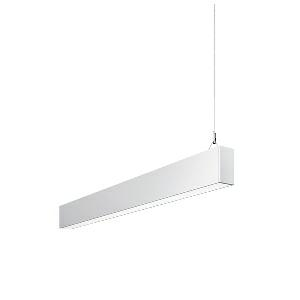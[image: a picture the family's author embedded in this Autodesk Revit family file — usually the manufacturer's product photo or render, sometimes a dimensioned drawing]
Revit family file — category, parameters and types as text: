
# Revit family: idoo_line_-_ilp_3000_840_d_end_00805690_544f
name_source: partatom
category: Lighting Fixtures
units: mm (PartAtom-declared; Revit-internal decimal feet)

## family parameters
Cut with Voids When Loaded = No
Host = Face
Light Source = No
Part Type = Normal
Room Calculation Point = No
Round Connector Dimension = Use Diameter
Shared = No

## types (1)
- IDOO.line - ILP 3000/840/D END (1 x LED, 3150 lm, 4000K)
    Apparent Load = 23 VA
    Approval mark = CE
    CIE Flux Codes = 66 91 98 40 100
    Color Rendering = 80-89
    Color Temperature = 4000K
    Control Gear = Electronic ballast
    Default Elevation = 1800 mm
    Description = ILP 3000/840/D|Suspended luminaire|light source: LED|connected load: 220-240 V, 50/60 Hz|Power consumption: approx. 23 W|standby: approx. 0,20|luminous flux: 3150 lm|luminous efficacy: 136 lm/W|light distribution: Direct/indirect|direct ratio: approx. 40 %|colour temperature: Cold white, ca. 4000 K|color rendering index (CRI): >= 80|chromaticity tolerance:  3 SDCM|System of protection: IP 40|technology: Continuously dimmable|luminaire body|material: Sectional aluminium|colour: White|lamp cover: Acrylic (PMMA), Clear|mains lead: 1,0 m With free stranded wires|Fastening: Steel cable 0.3 - 0.7 m|glare control: Prism aperture|luminance(L65): <= 2700 cd/m|unified glare rating(4H 8H): <=  16|special features: DALI Load 1x, TouchDIM - dimming via standard switch, Through-wired, up to 18 m on one mains connection, Flicker-free, Suitable as emergency lighting, Mechanical and electrical connection of the individual modules without tools|
    Frequency = 50 Hz
    Height = 110 mm
    Lamp = 1 x LED
    Lamp Light Flux = 3150 lm
    Lamp count = 1
    Length = 1128 mm
    Luminous efficacy = 137 lm/W
    Manufacturer = Waldmann
    ModVariant = No
    Model = 00805690
    Mounting Place = Ceiling
    Mounting Type = Pendant
    Number of Poles = 1
    OnlyDefault = Yes
    Power Factor = 1
    Product Name = IDOO.line - ILP 3000/840/D END
    Product group = Suspended luminaire
    ProductGroupID = 9
    Protection Class = Protection class I
    Protection Degree = IP 40
    RLX_Detail_Level = 1
    RLX_Emergency_Light_Flux = 0 lm
    RLX_Emergency_Type = 0
    RLX_Emergency_Type_DB = No
    RlxData = <blob elided: 18125 chars, md5=2649ad31>
    Socket = socket
    Standby Power = 0 W
    System Light Flux = 3150 lm
    System Power = 23 W
    Type Comments = Product without accessories
    Type Image = 113303000-00692573.jpg
    URL = http://relux.com
    VarID = ---
    Voltage = 230 V
    Voltage Range = 220-240 V
    Weight = 0.00 kg
    Width = 60 mm  [stored 0.19685 ft]

note: [stored X ft] marks values corroborated as IEEE doubles in the binary element streams (Revit-internal decimal feet)

## geometry (parser evidence)
native form markers: Blend x4, Sweep x13
no freeform markers — native parametric forms only
